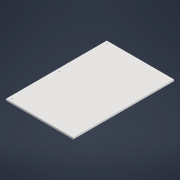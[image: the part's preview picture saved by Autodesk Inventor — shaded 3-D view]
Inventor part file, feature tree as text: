
AUTODESK INVENTOR PART (.ipt)
format: ipt  version: 2021 (Build 250183000, 183)  size: 138,240 bytes
history: native  units: mm
features: sketch x4, extrude x2, hole x2, other x1, fillet x1
ambient origin geometry x8: Origin, YZ Plane, XZ Plane, XY Plane, X Axis, Y Axis, Z Axis, Center Point
bodies: Body1 (feature_tree)
feature tree (10):
  other  "ソリッド1"
  extrude  "押し出し1"  Depth=155.0mm
  hole  "穴1"  [1 undecoded]
  extrude  "押し出し2"  Depth=4.0mm TaperAngle=0.0deg
  hole  "穴2"  [1 undecoded]
  fillet  "フィレット1"  Radius=5.0mm
  sketch  "スケッチ1"
  sketch  "スケッチ3"
  sketch  "スケッチ5"
  sketch  "スケッチ6"
note: 2 required parameter values undecoded (feature->parameter linkage not recoverable at this tier; creation-order binding heuristic only, values carry confidence <= 0.55)
